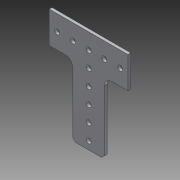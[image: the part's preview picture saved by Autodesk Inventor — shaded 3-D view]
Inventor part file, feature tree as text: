
AUTODESK INVENTOR PART (.ipt)
format: ipt  version: 2014 SP1 (Build 180222100, 222)  size: 166,400 bytes
history: native  units: in
note: dims shown in document units (in); Inventor stores cm internally (conversion verified against a paired STEP export)
features: other x2, extrude x1, imported_body x1, sketch x1
ambient origin geometry x8: Origin, YZ Plane, XZ Plane, XY Plane, X Axis, Y Axis, Z Axis, Center Point
bodies: Body1 (feature_tree)
feature tree (5):
  other  "Break-Corner1"
  other  "217-3547-STEP1"
  extrude  "Extrusion1"  Depth=0.75in
  imported_body  "Base1"
  sketch  "Sketch1"  dims[d0=0.75in d1=0.75in d2=1.0in d3=0.0in]
